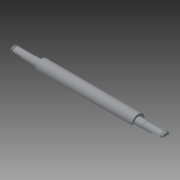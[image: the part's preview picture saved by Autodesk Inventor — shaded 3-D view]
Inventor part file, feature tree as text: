
AUTODESK INVENTOR PART (.ipt)
format: ipt  version: 2014 (Build 180170000, 170)  size: 123,904 bytes
history: native  units: mm
features: sketch x3, extrude x2, revolve x1, chamfer x1, mirror x1
ambient origin geometry x8: Origin, YZ Plane, XZ Plane, XY Plane, X Axis, Y Axis, Z Axis, Center Point
bodies: Solid1 (feature_tree)
feature tree (8):
  revolve  "Revolution1"  [1 undecoded]
  extrude  "Extrusion1"  Depth=7.0mm
  chamfer  "Chamfer1"  Distance=1.0mm
  extrude  "Extrusion2"  Depth=66.0mm
  mirror  "Mirror1"
  sketch  "Sketch1"  dims[d5=43.0mm d6=3.5mm]
  sketch  "Sketch2"  dims[d7=3.75mm d8=7.0mm]
  sketch  "Sketch3"  dims[d9=120.0deg d10=1.0mm d11=66.0mm d12=5.75mm d13=180.0deg d14=8.0mm d15=1.25mm d16=0.0mm d17=1.25mm d18=2.0mm d19=45.0deg d20=2.0mm d21=0.0mm]
note: 1 required parameter value undecoded (feature->parameter linkage not recoverable at this tier; creation-order binding heuristic only, values carry confidence <= 0.55)
